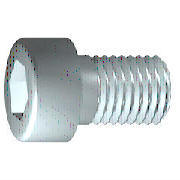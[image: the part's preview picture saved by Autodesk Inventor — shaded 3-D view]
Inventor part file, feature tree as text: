
AUTODESK INVENTOR PART (.ipt)
format: ipt  version: 2020 (Build 240168000, 168)  size: 192,000 bytes
history: native  units: mm (DEFAULTED — no unit token found)
features: sketch x2, other x1, extrude x1, plane x1, fillet x1
ambient origin geometry x7: Origin, YZ Plane, XY Plane, X Axis, Y Axis, Z Axis, Center Point
bodies: Solid1 (feature_tree)
feature tree (6):
  other  "Bryła"
  extrude  "Szczelina"  Depth=14.75mm
  plane  "Work Plane1"
  fillet  "Fillet2"  Radius=0.306825mm
  sketch  "Szkic1"
  sketch  "Szkic2"
